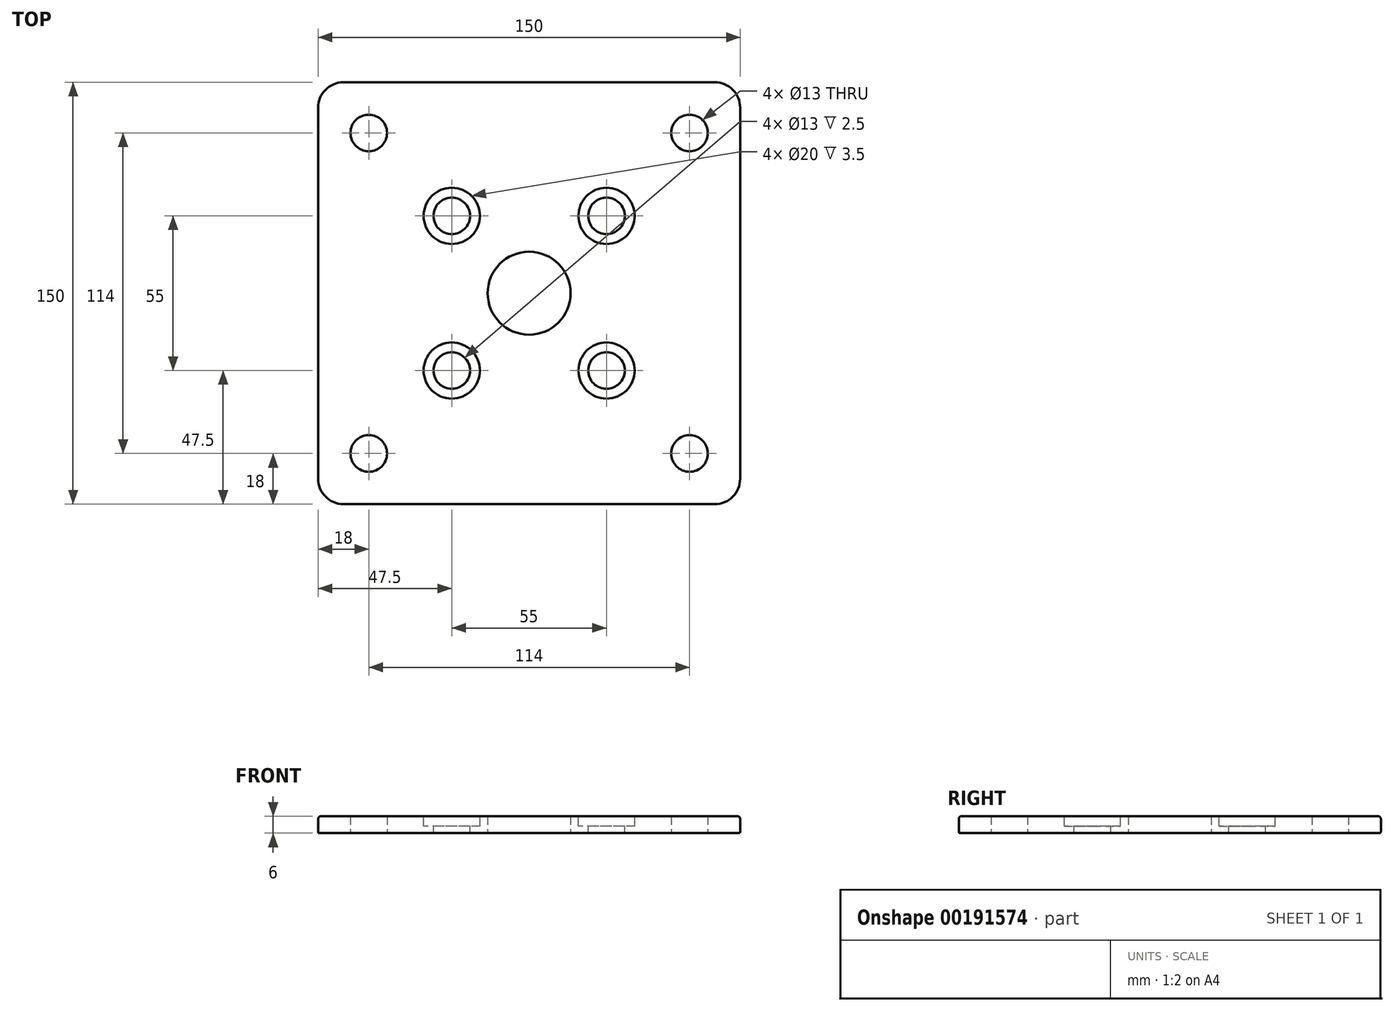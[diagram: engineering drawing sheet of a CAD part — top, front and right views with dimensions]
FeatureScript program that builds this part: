
annotation { "Feature Type Name" : "Feature", "Feature Type Description" : "" }
export const myFeature = defineFeature(function(context is Context, id is Id, definition is map)
    precondition{}
    {
        {
            var Q0;
            Q0=qCreatedBy(makeId("Top.planeOp"),FACE);
            var sketch = newSketch(context, id + "F0", { "sketchPlane" : qUnion([Q0])});
            skLineSegment(sketch, "E0.bottom", {"start": v(-75, 75) * mm, "end": v(75, 75) * mm});
            skLineSegment(sketch, "E0.top", {"start": v(-75, -75) * mm, "end": v(75, -75) * mm});
            skLineSegment(sketch, "E0.left", {"start": v(-75, 75) * mm, "end": v(-75, -75) * mm});
            skLineSegment(sketch, "E0.right", {"start": v(75, 75) * mm, "end": v(75, -75) * mm});
            skLineSegment(sketch, "E1", {"start": v(-75, 0) * mm, "end": v(75, 0) * mm, "construction": true});
            skLineSegment(sketch, "E2", {"start": v(0, 75) * mm, "end": v(0, -75) * mm, "construction": true});
            skCircle(sketch, "E3", {"center": v(0, 0) * mm, "radius": 14.75 * mm});
            skCircle(sketch, "E4", {"center": v(57, 57) * mm, "radius": 6.5 * mm});
            skCircle(sketch, "E5", {"center": v(57, -57) * mm, "radius": 6.5 * mm});
            skCircle(sketch, "E6", {"center": v(-57, -57) * mm, "radius": 6.5 * mm});
            skCircle(sketch, "E7", {"center": v(-57, 57) * mm, "radius": 6.5 * mm});
            skSolve(sketch);
        }
        {
            var Q0;
            Q0=makeQuery(id+"F0.imprint","IMPRINT",FACE,{"disambiguationData":[TD([[makeQuery(id+"F0.imprint","IMPRINT",EDGE,{"derivedFrom":sQuery(id+"F0.wireOp",EDGE,"E0.bottom")}),-1.0]])]});
            extrude(context, id + "F1", {"entities" : qUnion([Q0]), "depth" : 6 * mm});
        }
        {
            var Q0;
            Q0=makeQuery(id+"F1.opExtrude","SWEPT_EDGE",EDGE,{"disambiguationData":[OSD([sQuery(id+"F0.wireOp",EDGE,"E0.top"),sQuery(id+"F0.wireOp",EDGE,"E0.left")])]});
            var Q1;
            Q1=makeQuery(id+"F1.opExtrude","SWEPT_EDGE",EDGE,{"disambiguationData":[OSD([sQuery(id+"F0.wireOp",EDGE,"E0.bottom"),sQuery(id+"F0.wireOp",EDGE,"E0.left")])]});
            var Q2;
            Q2=makeQuery(id+"F1.opExtrude","SWEPT_EDGE",EDGE,{"disambiguationData":[OSD([sQuery(id+"F0.wireOp",EDGE,"E0.top"),sQuery(id+"F0.wireOp",EDGE,"E0.right")])]});
            var Q3;
            Q3=makeQuery(id+"F1.opExtrude","SWEPT_EDGE",EDGE,{"disambiguationData":[OSD([sQuery(id+"F0.wireOp",EDGE,"E0.bottom"),sQuery(id+"F0.wireOp",EDGE,"E0.right")])]});
            fillet(context, id + "F2", {"entities" : qUnion([Q0, Q1, Q2, Q3]), "radius" : 9 * mm, "tangentPropagation" : true, "allowEdgeOverflow" : false});
        }
        {
            var Q0;
            Q0=makeQuery(id+"F1.opExtrude","CAP_FACE",FACE,{"disambiguationData":[OSD([sQuery(id+"F0.wireOp",EDGE,"E0.bottom"),sQuery(id+"F0.wireOp",EDGE,"E0.top"),sQuery(id+"F0.wireOp",EDGE,"E0.left"),sQuery(id+"F0.wireOp",EDGE,"E0.right"),sQuery(id+"F0.wireOp",EDGE,"E3"),sQuery(id+"F0.wireOp",EDGE,"E4"),sQuery(id+"F0.wireOp",EDGE,"E5"),sQuery(id+"F0.wireOp",EDGE,"E6"),sQuery(id+"F0.wireOp",EDGE,"E7")])],"isStart":false});
            var sketch = newSketch(context, id + "F3", { "sketchPlane" : qUnion([Q0])});
            skPoint(sketch, "E8", {"position": v(-27.5, 27.5) * mm});
            skPoint(sketch, "E9", {"position": v(27.5, 27.5) * mm});
            skPoint(sketch, "E10", {"position": v(-27.5, -27.5) * mm});
            skPoint(sketch, "E11", {"position": v(27.5, -27.5) * mm});
            skSolve(sketch);
        }
        {
            var Q0;
            Q0=sQuery(id+"F3.wireOp",VERTEX,"E8");
            var Q1;
            Q1=sQuery(id+"F3.wireOp",VERTEX,"E9");
            var Q2;
            Q2=sQuery(id+"F3.wireOp",VERTEX,"E11");
            var Q3;
            Q3=sQuery(id+"F3.wireOp",VERTEX,"E10");
            var Q4;
            Q4=makeQuery(id+"F1.opExtrude","SWEPT_BODY",BODY,{"disambiguationData":[OSD([sQuery(id+"F0.wireOp",EDGE,"E0.bottom"),sQuery(id+"F0.wireOp",EDGE,"E0.top"),sQuery(id+"F0.wireOp",EDGE,"E0.left"),sQuery(id+"F0.wireOp",EDGE,"E0.right"),sQuery(id+"F0.wireOp",EDGE,"E3"),sQuery(id+"F0.wireOp",EDGE,"E4"),sQuery(id+"F0.wireOp",EDGE,"E5"),sQuery(id+"F0.wireOp",EDGE,"E6"),sQuery(id+"F0.wireOp",EDGE,"E7")])]});
            hole(context, id + "F4", {"style" : HoleStyle.C_BORE, "endStyle" : HoleEndStyle.THROUGH, "holeDiameter" : 13 * mm, "cBoreDiameter" : 20 * mm, "cBoreDepth" : 3.5 * mm, "locations" : qUnion([Q0, Q1, Q2, Q3]), "scope" : qUnion([Q4]), "isTappedThrough" : true});
        }
        {
            var Q0;
            {var subQ0=sQuery(id+"F0.wireOp",EDGE,"E0.left");var subQ1=sQuery(id+"F0.wireOp",EDGE,"E0.bottom");Q0=makeQuery(id+"F2.opFillet","BLEND_EDGE",EDGE,{"blendedFrom":[makeQuery(id+"F1.opExtrude","SWEPT_EDGE",EDGE,{"disambiguationData":[OSD([subQ1,subQ0])]}),makeQuery(id+"F1.opExtrude","CAP_FACE",FACE,{"disambiguationData":[OSD([subQ1,sQuery(id+"F0.wireOp",EDGE,"E0.top"),subQ0,sQuery(id+"F0.wireOp",EDGE,"E0.right"),sQuery(id+"F0.wireOp",EDGE,"E3"),sQuery(id+"F0.wireOp",EDGE,"E4"),sQuery(id+"F0.wireOp",EDGE,"E5"),sQuery(id+"F0.wireOp",EDGE,"E6"),sQuery(id+"F0.wireOp",EDGE,"E7")])],"isStart":false})],"blendedInto":[makeQuery(id+"F1.opExtrude","CAP_FACE",FACE,{"disambiguationData":[OSD([subQ1,sQuery(id+"F0.wireOp",EDGE,"E0.top"),subQ0,sQuery(id+"F0.wireOp",EDGE,"E0.right"),sQuery(id+"F0.wireOp",EDGE,"E3"),sQuery(id+"F0.wireOp",EDGE,"E4"),sQuery(id+"F0.wireOp",EDGE,"E5"),sQuery(id+"F0.wireOp",EDGE,"E6"),sQuery(id+"F0.wireOp",EDGE,"E7")])],"isStart":false})]});}
            var Q1;
            Q1=makeQuery(id+"F1.opExtrude","CAP_EDGE",EDGE,{"disambiguationData":[OSD([sQuery(id+"F0.wireOp",EDGE,"E0.bottom")])],"isStart":false});
            var Q2;
            Q2=makeQuery(id+"F1.opExtrude","CAP_EDGE",EDGE,{"disambiguationData":[OSD([sQuery(id+"F0.wireOp",EDGE,"E0.left")])],"isStart":false});
            fillet(context, id + "F5", {"entities" : qUnion([Q0, Q1, Q2]), "radius" : 1 * mm, "tangentPropagation" : true, "allowEdgeOverflow" : false});
        }
        {
            var Q0;
            Q0=makeQuery(id+"F1.opExtrude","SWEPT_FACE",FACE,{"disambiguationData":[OSD([sQuery(id+"F0.wireOp",EDGE,"E0.left")])]});
            var Q1;
            Q1=makeQuery(id+"F1.opExtrude","SWEPT_FACE",FACE,{"disambiguationData":[OSD([sQuery(id+"F0.wireOp",EDGE,"E0.top")])]});
            fillet(context, id + "F6", {"entities" : qUnion([Q0, Q1]), "radius" : .5 * mm, "tangentPropagation" : true, "allowEdgeOverflow" : false});
        }
    });
